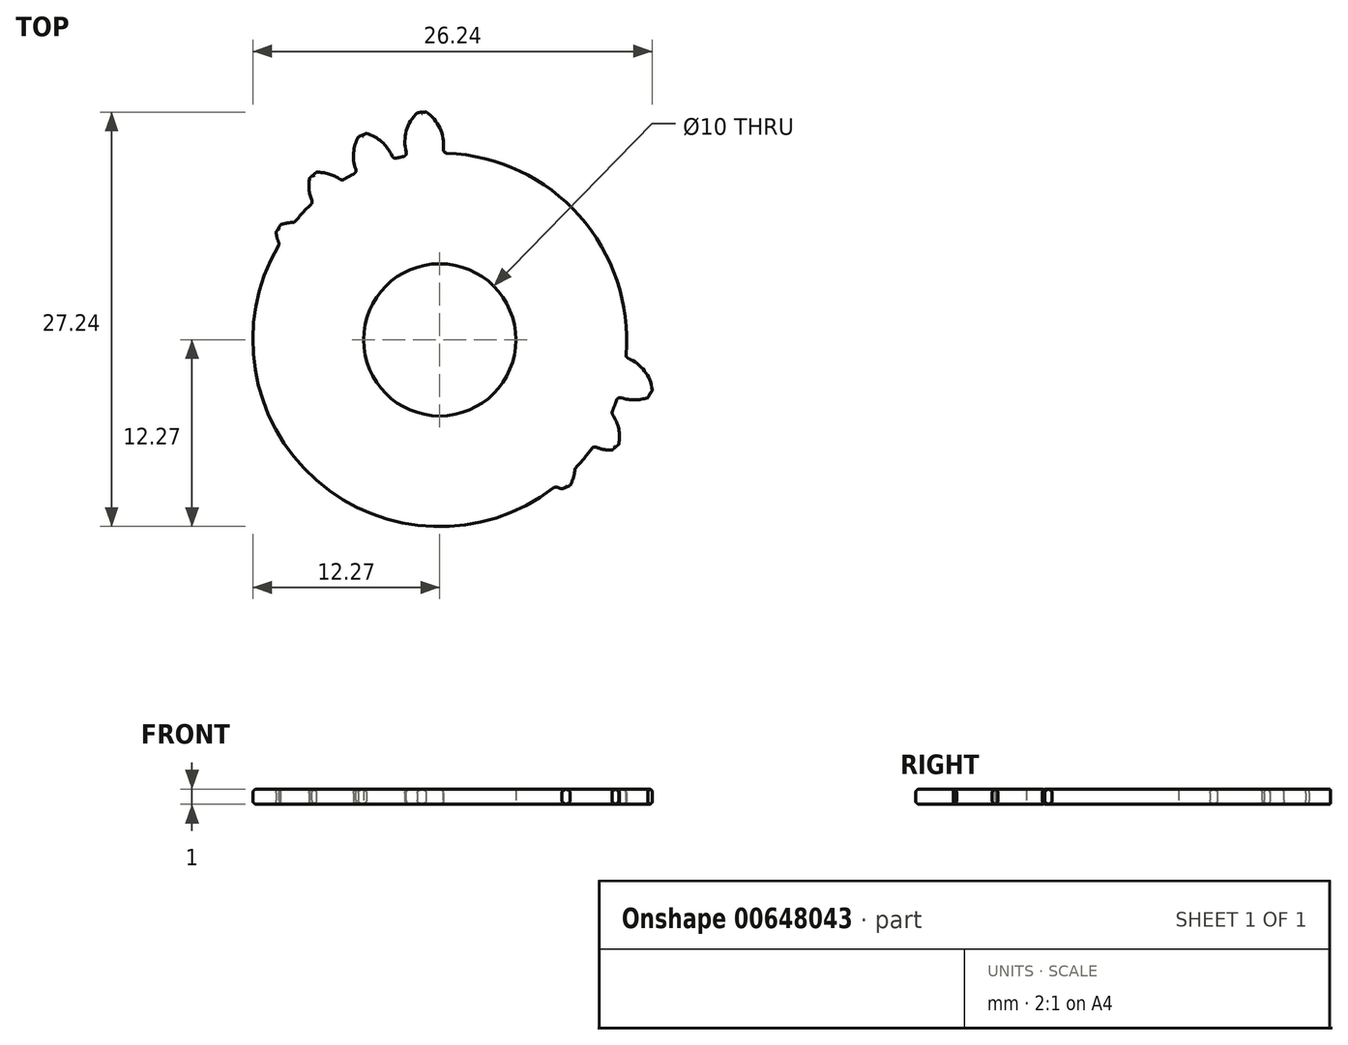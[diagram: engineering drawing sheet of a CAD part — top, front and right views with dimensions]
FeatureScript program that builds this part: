
annotation { "Feature Type Name" : "Feature", "Feature Type Description" : "" }
export const myFeature = defineFeature(function(context is Context, id is Id, definition is map)
    precondition{}
    {
        {
            assignVariable(context, id + "F0", {"name" : "GearDepth", "anyValue" : 1});
        }
        {
            assignVariable(context, id + "F1", {"name" : "TeethFillet", "anyValue" : getVariable(context, 'GearDepth') * .25});
        }
        {
            var Q0;
            Q0=qCreatedBy(makeId("Top.planeOp"),FACE);
            var sketch = newSketch(context, id + "F2", { "sketchPlane" : qUnion([Q0])});
            skCircle(sketch, "E0", {"center": v(0, 0) * mm, "radius": 12.27 * mm});
            skCircle(sketch, "E1", {"center": v(0, 0) * mm, "radius": 13.64 * mm, "construction": true});
            skCircle(sketch, "E2", {"center": v(0, 0) * mm, "radius": 15 * mm, "construction": true});
            skLineSegment(sketch, "E3", {"start": v(0, 0) * mm, "end": v(0, 17.6) * mm, "construction": true});
            skLineSegment(sketch, "E4", {"start": v(0, 0) * mm, "end": v(-1.42, 18) * mm, "construction": true});
            skLineSegment(sketch, "E5", {"start": v(0, 13.64) * mm, "end": v(-10.54, 13.64) * mm, "construction": true});
            skLineSegment(sketch, "E6", {"start": v(0, 13.64) * mm, "end": v(-10.3, 9.9) * mm, "construction": true});
            skCircle(sketch, "E7", {"center": v(0, 13.64) * mm, "radius": 3.4 * mm, "construction": true});
            skCircle(sketch, "E8", {"center": v(-3.2, 12.47) * mm, "radius": 3.4 * mm, "construction": true});
            skArc(sketch, "E9", {"start": v(-6.4, 13.64) * mm, "mid": v(-6.42, 13.6) * mm, "end": v(-6.44, 13.55) * mm});
            skArc(sketch, "E10.trimOffspring", {"start": v(0.2, 12.27) * mm, "mid": v(0.07, 13.79) * mm, "end": v(-0.89, 14.97) * mm});
            skArc(sketch, "E11.MirrorCS", {"start": v(-2.12, 12.09) * mm, "mid": v(-2.22, 13.6) * mm, "end": v(-1.46, 14.93) * mm});
            skLineSegment(sketch, "E12", {"start": v(-1.46, 14.93) * mm, "end": v(-0.89, 14.97) * mm});
            skArc(sketch, "E13.1.0", {"start": v(-2.94, 11.33) * mm, "mid": v(-3.54, 12.73) * mm, "end": v(-4.81, 13.56) * mm});
            skLineSegment(sketch, "E13.1.1", {"start": v(-5.35, 13.34) * mm, "end": v(-4.81, 13.56) * mm});
            skArc(sketch, "E13.1.2", {"start": v(-5.09, 10.44) * mm, "mid": v(-5.66, 11.85) * mm, "end": v(-5.35, 13.34) * mm});
            skArc(sketch, "E13.2.0", {"start": v(-5.64, 9.46) * mm, "mid": v(-6.64, 10.6) * mm, "end": v(-8.1, 11) * mm});
            skLineSegment(sketch, "E13.2.1", {"start": v(-8.55, 10.63) * mm, "end": v(-8.1, 11) * mm});
            skArc(sketch, "E13.2.2", {"start": v(-7.4, 7.95) * mm, "mid": v(-8.38, 9.12) * mm, "end": v(-8.55, 10.63) * mm});
            skArc(sketch, "E13.3.0", {"start": v(-7.63, 6.85) * mm, "mid": v(-8.93, 7.63) * mm, "end": v(-10.45, 7.56) * mm});
            skLineSegment(sketch, "E13.3.1", {"start": v(-10.75, 7.07) * mm, "end": v(-10.45, 7.56) * mm});
            skArc(sketch, "E13.3.2", {"start": v(-8.84, 4.87) * mm, "mid": v(-10.13, 5.68) * mm, "end": v(-10.75, 7.07) * mm});
            skArc(sketch, "E13.4.0", {"start": v(-8.7, 3.75) * mm, "mid": v(-10.2, 4.1) * mm, "end": v(-11.62, 3.55) * mm});
            skLineSegment(sketch, "E13.4.1", {"start": v(-11.75, 3) * mm, "end": v(-11.62, 3.55) * mm});
            skArc(sketch, "E13.4.2", {"start": v(-9.25, 1.5) * mm, "mid": v(-10.73, 1.86) * mm, "end": v(-11.75, 3) * mm});
            skArc(sketch, "E13.5.0", {"start": v(-8.78, 0.47) * mm, "mid": v(-10.3, 0.34) * mm, "end": v(-11.49, -0.61) * mm});
            skLineSegment(sketch, "E13.5.1", {"start": v(-11.44, -1.19) * mm, "end": v(-11.49, -0.61) * mm});
            skArc(sketch, "E13.5.2", {"start": v(-8.6, -1.84) * mm, "mid": v(-10.12, -1.95) * mm, "end": v(-11.44, -1.19) * mm});
            skArc(sketch, "E13.6.0", {"start": v(-7.84, -2.67) * mm, "mid": v(-9.24, -3.26) * mm, "end": v(-10.07, -4.54) * mm});
            skLineSegment(sketch, "E13.6.1", {"start": v(-9.85, -5.07) * mm, "end": v(-10.07, -4.54) * mm});
            skArc(sketch, "E13.6.2", {"start": v(-6.95, -4.81) * mm, "mid": v(-8.36, -5.38) * mm, "end": v(-9.85, -5.07) * mm});
            skArc(sketch, "E13.7.0", {"start": v(-5.97, -5.36) * mm, "mid": v(-7.12, -6.36) * mm, "end": v(-7.52, -7.83) * mm});
            skLineSegment(sketch, "E13.7.1", {"start": v(-7.14, -8.27) * mm, "end": v(-7.52, -7.83) * mm});
            skArc(sketch, "E13.7.2", {"start": v(-4.46, -7.13) * mm, "mid": v(-5.63, -8.1) * mm, "end": v(-7.14, -8.27) * mm});
            skArc(sketch, "E13.8.0", {"start": v(-3.36, -7.35) * mm, "mid": v(-4.15, -8.66) * mm, "end": v(-4.07, -10.18) * mm});
            skLineSegment(sketch, "E13.8.1", {"start": v(-3.58, -10.48) * mm, "end": v(-4.07, -10.18) * mm});
            skArc(sketch, "E13.8.2", {"start": v(-1.38, -8.57) * mm, "mid": v(-2.19, -9.86) * mm, "end": v(-3.58, -10.48) * mm});
            skArc(sketch, "E13.9.0", {"start": v(-0.27, -8.43) * mm, "mid": v(-0.6, -9.92) * mm, "end": v(-0.06, -11.34) * mm});
            skLineSegment(sketch, "E13.9.1", {"start": v(0.5, -11.48) * mm, "end": v(-0.06, -11.34) * mm});
            skArc(sketch, "E13.9.2", {"start": v(2, -8.98) * mm, "mid": v(1.63, -10.45) * mm, "end": v(0.5, -11.48) * mm});
            skArc(sketch, "E13.10.0", {"start": v(3.01, -8.5) * mm, "mid": v(3.15, -10.03) * mm, "end": v(4.1, -11.21) * mm});
            skLineSegment(sketch, "E13.10.1", {"start": v(4.68, -11.17) * mm, "end": v(4.1, -11.21) * mm});
            skArc(sketch, "E13.10.2", {"start": v(5.33, -8.33) * mm, "mid": v(5.44, -9.84) * mm, "end": v(4.68, -11.17) * mm});
            skArc(sketch, "E13.11.0", {"start": v(6.16, -7.56) * mm, "mid": v(6.75, -8.97) * mm, "end": v(8.03, -9.8) * mm});
            skLineSegment(sketch, "E13.11.1", {"start": v(8.56, -9.58) * mm, "end": v(8.03, -9.8) * mm});
            skArc(sketch, "E13.11.2", {"start": v(8.3, -6.68) * mm, "mid": v(8.87, -8.09) * mm, "end": v(8.56, -9.58) * mm});
            skArc(sketch, "E13.12.0", {"start": v(8.85, -5.7) * mm, "mid": v(9.85, -6.85) * mm, "end": v(11.32, -7.24) * mm});
            skLineSegment(sketch, "E13.12.1", {"start": v(11.76, -6.87) * mm, "end": v(11.32, -7.24) * mm});
            skArc(sketch, "E13.12.2", {"start": v(10.62, -4.19) * mm, "mid": v(11.6, -5.35) * mm, "end": v(11.76, -6.87) * mm});
            skArc(sketch, "E13.13.0", {"start": v(10.84, -3.09) * mm, "mid": v(12.14, -3.87) * mm, "end": v(13.67, -3.8) * mm});
            skLineSegment(sketch, "E13.13.1", {"start": v(13.97, -3.3) * mm, "end": v(13.67, -3.8) * mm});
            skArc(sketch, "E13.13.2", {"start": v(12.05, -1.1) * mm, "mid": v(13.35, -1.91) * mm, "end": v(13.97, -3.3) * mm});
            skArc(sketch, "E13.14.0", {"start": v(11.92, 0) * mm, "mid": v(13.4, -0.33) * mm, "end": v(14.83, 0.2) * mm});
            skLineSegment(sketch, "E13.14.1", {"start": v(14.96, 0.77) * mm, "end": v(14.83, 0.2) * mm});
            skArc(sketch, "E13.14.2", {"start": v(12.47, 2.27) * mm, "mid": v(13.94, 1.9) * mm, "end": v(14.96, 0.77) * mm});
            skArc(sketch, "E13.15.0", {"start": v(12, 3.29) * mm, "mid": v(13.51, 3.42) * mm, "end": v(14.7, 4.38) * mm});
            skLineSegment(sketch, "E13.15.1", {"start": v(14.65, 4.95) * mm, "end": v(14.7, 4.38) * mm});
            skArc(sketch, "E13.15.2", {"start": v(11.81, 5.6) * mm, "mid": v(13.33, 5.71) * mm, "end": v(14.65, 4.95) * mm});
            skArc(sketch, "E13.16.0", {"start": v(11.05, 6.43) * mm, "mid": v(12.45, 7.03) * mm, "end": v(13.29, 8.3) * mm});
            skLineSegment(sketch, "E13.16.1", {"start": v(13.07, 8.83) * mm, "end": v(13.29, 8.3) * mm});
            skArc(sketch, "E13.16.2", {"start": v(10.16, 8.58) * mm, "mid": v(11.58, 9.15) * mm, "end": v(13.07, 8.83) * mm});
            skArc(sketch, "E13.17.0", {"start": v(9.19, 9.13) * mm, "mid": v(10.33, 10.13) * mm, "end": v(10.73, 11.6) * mm});
            skLineSegment(sketch, "E13.17.1", {"start": v(10.36, 12.03) * mm, "end": v(10.73, 11.6) * mm});
            skArc(sketch, "E13.17.2", {"start": v(7.68, 10.9) * mm, "mid": v(8.84, 11.87) * mm, "end": v(10.36, 12.03) * mm});
            skArc(sketch, "E13.18.0", {"start": v(6.58, 11.11) * mm, "mid": v(7.36, 12.42) * mm, "end": v(7.28, 13.94) * mm});
            skLineSegment(sketch, "E13.18.1", {"start": v(6.8, 14.24) * mm, "end": v(7.28, 13.94) * mm});
            skArc(sketch, "E13.18.2", {"start": v(4.6, 12.33) * mm, "mid": v(5.4, 13.62) * mm, "end": v(6.8, 14.24) * mm});
            skArc(sketch, "E13.19.0", {"start": v(3.48, 12.2) * mm, "mid": v(3.82, 13.68) * mm, "end": v(3.28, 15.1) * mm});
            skLineSegment(sketch, "E13.19.1", {"start": v(2.72, 15.24) * mm, "end": v(3.28, 15.1) * mm});
            skArc(sketch, "E13.19.2", {"start": v(1.22, 12.74) * mm, "mid": v(1.59, 14.22) * mm, "end": v(2.72, 15.24) * mm});
            skPoint(sketch, "E13.center", {"position": v(1.6, 1.88) * mm});
            skCircle(sketch, "E14", {"center": v(0, 0) * mm, "radius": 5 * mm});
            skSolve(sketch);
        }
        {
            var Q0;
            {var subQ0=sQuery(id+"F2.wireOp",EDGE,"E10.trimOffspring");Q0=makeQuery(id+"F2.imprint","IMPRINT",FACE,{"disambiguationData":[TD([[makeQuery(id+"F2.imprint","IMPRINT",EDGE,{"derivedFrom":subQ0}),1.0]])]});}
            var Q1;
            {var subQ0=sQuery(id+"F2.wireOp",EDGE,"E0");var subQ1=makeQuery(id+"F2.imprint","INTERSECT",VERTEX,{"derivedFrom":[subQ0,sQuery(id+"F2.wireOp",EDGE,"E10.trimOffspring")]});Q1=makeQuery(id+"F2.imprint","IMPRINT",FACE,{"disambiguationData":[TD([[makeQuery(id+"F2.imprint","IMPRINT",EDGE,{"disambiguationData":[TD([[subQ1,-1.0]])],"derivedFrom":subQ0}),1.0]])]});}
            var Q2;
            {var subQ0=sQuery(id+"F2.wireOp",EDGE,"E13.1.0");Q2=makeQuery(id+"F2.imprint","IMPRINT",FACE,{"disambiguationData":[TD([[makeQuery(id+"F2.imprint","IMPRINT",EDGE,{"derivedFrom":subQ0}),1.0]])]});}
            var Q3;
            {var subQ0=sQuery(id+"F2.wireOp",EDGE,"E13.2.0");Q3=makeQuery(id+"F2.imprint","IMPRINT",FACE,{"disambiguationData":[TD([[makeQuery(id+"F2.imprint","IMPRINT",EDGE,{"derivedFrom":subQ0}),1.0]])]});}
            var Q4;
            {var subQ0=sQuery(id+"F2.wireOp",EDGE,"E13.3.0");Q4=makeQuery(id+"F2.imprint","IMPRINT",FACE,{"disambiguationData":[TD([[makeQuery(id+"F2.imprint","IMPRINT",EDGE,{"derivedFrom":subQ0}),1.0]])]});}
            var Q5;
            {var subQ0=sQuery(id+"F2.wireOp",EDGE,"E13.4.0");Q5=makeQuery(id+"F2.imprint","IMPRINT",FACE,{"disambiguationData":[TD([[makeQuery(id+"F2.imprint","IMPRINT",EDGE,{"derivedFrom":subQ0}),1.0]])]});}
            var Q6;
            {var subQ0=sQuery(id+"F2.wireOp",EDGE,"E13.5.0");Q6=makeQuery(id+"F2.imprint","IMPRINT",FACE,{"disambiguationData":[TD([[makeQuery(id+"F2.imprint","IMPRINT",EDGE,{"derivedFrom":subQ0}),1.0]])]});}
            var Q7;
            {var subQ0=sQuery(id+"F2.wireOp",EDGE,"E13.6.0");Q7=makeQuery(id+"F2.imprint","IMPRINT",FACE,{"disambiguationData":[TD([[makeQuery(id+"F2.imprint","IMPRINT",EDGE,{"derivedFrom":subQ0}),1.0]])]});}
            var Q8;
            {var subQ0=sQuery(id+"F2.wireOp",EDGE,"E13.7.0");Q8=makeQuery(id+"F2.imprint","IMPRINT",FACE,{"disambiguationData":[TD([[makeQuery(id+"F2.imprint","IMPRINT",EDGE,{"derivedFrom":subQ0}),1.0]])]});}
            var Q9;
            {var subQ0=sQuery(id+"F2.wireOp",EDGE,"E13.8.0");Q9=makeQuery(id+"F2.imprint","IMPRINT",FACE,{"disambiguationData":[TD([[makeQuery(id+"F2.imprint","IMPRINT",EDGE,{"derivedFrom":subQ0}),1.0]])]});}
            var Q10;
            {var subQ0=sQuery(id+"F2.wireOp",EDGE,"E13.9.0");Q10=makeQuery(id+"F2.imprint","IMPRINT",FACE,{"disambiguationData":[TD([[makeQuery(id+"F2.imprint","IMPRINT",EDGE,{"derivedFrom":subQ0}),1.0]])]});}
            var Q11;
            {var subQ0=sQuery(id+"F2.wireOp",EDGE,"E13.10.0");Q11=makeQuery(id+"F2.imprint","IMPRINT",FACE,{"disambiguationData":[TD([[makeQuery(id+"F2.imprint","IMPRINT",EDGE,{"derivedFrom":subQ0}),1.0]])]});}
            var Q12;
            {var subQ0=sQuery(id+"F2.wireOp",EDGE,"E13.11.0");Q12=makeQuery(id+"F2.imprint","IMPRINT",FACE,{"disambiguationData":[TD([[makeQuery(id+"F2.imprint","IMPRINT",EDGE,{"derivedFrom":subQ0}),1.0]])]});}
            var Q13;
            {var subQ0=sQuery(id+"F2.wireOp",EDGE,"E13.12.0");Q13=makeQuery(id+"F2.imprint","IMPRINT",FACE,{"disambiguationData":[TD([[makeQuery(id+"F2.imprint","IMPRINT",EDGE,{"derivedFrom":subQ0}),1.0]])]});}
            var Q14;
            {var subQ0=sQuery(id+"F2.wireOp",EDGE,"E13.13.0");Q14=makeQuery(id+"F2.imprint","IMPRINT",FACE,{"disambiguationData":[TD([[makeQuery(id+"F2.imprint","IMPRINT",EDGE,{"derivedFrom":subQ0}),1.0]])]});}
            var Q15;
            {var subQ0=sQuery(id+"F2.wireOp",EDGE,"E13.14.0");Q15=makeQuery(id+"F2.imprint","IMPRINT",FACE,{"disambiguationData":[TD([[makeQuery(id+"F2.imprint","IMPRINT",EDGE,{"derivedFrom":subQ0}),1.0]])]});}
            var Q16;
            {var subQ0=sQuery(id+"F2.wireOp",EDGE,"E13.15.0");Q16=makeQuery(id+"F2.imprint","IMPRINT",FACE,{"disambiguationData":[TD([[makeQuery(id+"F2.imprint","IMPRINT",EDGE,{"derivedFrom":subQ0}),1.0]])]});}
            var Q17;
            {var subQ0=sQuery(id+"F2.wireOp",EDGE,"E13.16.0");Q17=makeQuery(id+"F2.imprint","IMPRINT",FACE,{"disambiguationData":[TD([[makeQuery(id+"F2.imprint","IMPRINT",EDGE,{"derivedFrom":subQ0}),1.0]])]});}
            var Q18;
            {var subQ0=sQuery(id+"F2.wireOp",EDGE,"E13.17.0");Q18=makeQuery(id+"F2.imprint","IMPRINT",FACE,{"disambiguationData":[TD([[makeQuery(id+"F2.imprint","IMPRINT",EDGE,{"derivedFrom":subQ0}),1.0]])]});}
            var Q19;
            {var subQ0=sQuery(id+"F2.wireOp",EDGE,"E13.18.0");Q19=makeQuery(id+"F2.imprint","IMPRINT",FACE,{"disambiguationData":[TD([[makeQuery(id+"F2.imprint","IMPRINT",EDGE,{"derivedFrom":subQ0}),1.0]])]});}
            var Q20;
            {var subQ0=sQuery(id+"F2.wireOp",EDGE,"E13.19.0");Q20=makeQuery(id+"F2.imprint","IMPRINT",FACE,{"disambiguationData":[TD([[makeQuery(id+"F2.imprint","IMPRINT",EDGE,{"derivedFrom":subQ0}),1.0]])]});}
            var Q21;
            Q21=sQuery(id+"F2.wireOp",EDGE,"E0");
            var Q22;
            Q22=sQuery(id+"F2.wireOp",EDGE,"E10.trimOffspring");
            var Q23;
            Q23=sQuery(id+"F2.wireOp",EDGE,"E12");
            var Q24;
            Q24=sQuery(id+"F2.wireOp",EDGE,"E11.MirrorCS");
            extrude(context, id + "F3", {"entities" : qUnion([Q0, Q1, Q2, Q3, Q4, Q5, Q6, Q7, Q8, Q9, Q10, Q11, Q12, Q13, Q14, Q15, Q16, Q17, Q18, Q19, Q20]), "surfaceEntities" : qUnion([Q21, Q22, Q23, Q24]), "depth" : (getVariable(context, 'GearDepth')) * mm, "offsetDistance" : 25 * mm});
        }
        {
            var Q0;
            Q0=makeQuery(id+"F3.opExtrude","CAP_EDGE",EDGE,{"disambiguationData":[OSD([sQuery(id+"F2.wireOp",EDGE,"E13.5.2")])],"isStart":false});
            var Q1;
            Q1=makeQuery(id+"F3.opExtrude","CAP_EDGE",EDGE,{"disambiguationData":[OSD([sQuery(id+"F2.wireOp",EDGE,"E13.5.1")])],"isStart":false});
            var Q2;
            {var subQ0=sQuery(id+"F2.wireOp",EDGE,"E0");Q2=makeQuery(id+"F3.opExtrude","CAP_EDGE",EDGE,{"disambiguationData":[OSD([subQ0]),TDD([makeQuery(id+"F2.imprint","IMPRINT",EDGE,{"disambiguationData":[TD([[makeQuery(id+"F2.imprint","INTERSECT",VERTEX,{"derivedFrom":[subQ0,sQuery(id+"F2.wireOp",EDGE,"E13.5.2")]}),-1.0]])],"derivedFrom":subQ0})])],"isStart":false});}
            var Q3;
            Q3=makeQuery(id+"F3.opExtrude","CAP_EDGE",EDGE,{"disambiguationData":[OSD([sQuery(id+"F2.wireOp",EDGE,"E13.6.0")])],"isStart":false});
            var Q4;
            Q4=makeQuery(id+"F3.opExtrude","CAP_EDGE",EDGE,{"disambiguationData":[OSD([sQuery(id+"F2.wireOp",EDGE,"E13.6.1")])],"isStart":false});
            var Q5;
            Q5=makeQuery(id+"F3.opExtrude","CAP_EDGE",EDGE,{"disambiguationData":[OSD([sQuery(id+"F2.wireOp",EDGE,"E13.6.2")])],"isStart":false});
            var Q6;
            {var subQ0=sQuery(id+"F2.wireOp",EDGE,"E0");Q6=makeQuery(id+"F3.opExtrude","SWEPT_FACE",FACE,{"disambiguationData":[OSD([subQ0]),TDD([makeQuery(id+"F2.imprint","IMPRINT",EDGE,{"disambiguationData":[TD([[makeQuery(id+"F2.imprint","INTERSECT",VERTEX,{"derivedFrom":[subQ0,sQuery(id+"F2.wireOp",EDGE,"E13.6.2")]}),-1.0]])],"derivedFrom":subQ0})])]});}
            var Q7;
            {var subQ0=sQuery(id+"F2.wireOp",EDGE,"E0");Q7=makeQuery(id+"F3.opExtrude","CAP_EDGE",EDGE,{"disambiguationData":[OSD([subQ0]),TDD([makeQuery(id+"F2.imprint","IMPRINT",EDGE,{"disambiguationData":[TD([[makeQuery(id+"F2.imprint","INTERSECT",VERTEX,{"derivedFrom":[subQ0,sQuery(id+"F2.wireOp",EDGE,"E13.6.2")]}),-1.0]])],"derivedFrom":subQ0})])],"isStart":false});}
            var Q8;
            Q8=makeQuery(id+"F3.opExtrude","CAP_EDGE",EDGE,{"disambiguationData":[OSD([sQuery(id+"F2.wireOp",EDGE,"E13.7.2")])],"isStart":true});
            var Q9;
            {var subQ0=sQuery(id+"F2.wireOp",EDGE,"E0");Q9=makeQuery(id+"F3.opExtrude","CAP_EDGE",EDGE,{"disambiguationData":[OSD([subQ0]),TDD([makeQuery(id+"F2.imprint","IMPRINT",EDGE,{"disambiguationData":[TD([[makeQuery(id+"F2.imprint","INTERSECT",VERTEX,{"derivedFrom":[subQ0,sQuery(id+"F2.wireOp",EDGE,"E13.7.2")]}),-1.0]])],"derivedFrom":subQ0})])],"isStart":true});}
            var Q10;
            Q10=makeQuery(id+"F3.opExtrude","CAP_EDGE",EDGE,{"disambiguationData":[OSD([sQuery(id+"F2.wireOp",EDGE,"E13.7.2")])],"isStart":false});
            var Q11;
            {var subQ0=sQuery(id+"F2.wireOp",EDGE,"E0");Q11=makeQuery(id+"F3.opExtrude","CAP_EDGE",EDGE,{"disambiguationData":[OSD([subQ0]),TDD([makeQuery(id+"F2.imprint","IMPRINT",EDGE,{"disambiguationData":[TD([[makeQuery(id+"F2.imprint","INTERSECT",VERTEX,{"derivedFrom":[subQ0,sQuery(id+"F2.wireOp",EDGE,"E13.7.2")]}),-1.0]])],"derivedFrom":subQ0})])],"isStart":false});}
            var Q12;
            Q12=makeQuery(id+"F3.opExtrude","CAP_EDGE",EDGE,{"disambiguationData":[OSD([sQuery(id+"F2.wireOp",EDGE,"E13.8.0")])],"isStart":false});
            var Q13;
            {var subQ0=sQuery(id+"F2.wireOp",EDGE,"E0");Q13=makeQuery(id+"F3.opExtrude","SWEPT_FACE",FACE,{"disambiguationData":[OSD([subQ0]),TDD([makeQuery(id+"F2.imprint","IMPRINT",EDGE,{"disambiguationData":[TD([[makeQuery(id+"F2.imprint","INTERSECT",VERTEX,{"derivedFrom":[subQ0,sQuery(id+"F2.wireOp",EDGE,"E13.7.2")]}),-1.0]])],"derivedFrom":subQ0})])]});}
            var Q14;
            Q14=makeQuery(id+"F3.opExtrude","CAP_EDGE",EDGE,{"disambiguationData":[OSD([sQuery(id+"F2.wireOp",EDGE,"E13.6.0")])],"isStart":true});
            var Q15;
            Q15=makeQuery(id+"F3.opExtrude","CAP_EDGE",EDGE,{"disambiguationData":[OSD([sQuery(id+"F2.wireOp",EDGE,"E13.8.2")])],"isStart":false});
            var Q16;
            {var subQ0=sQuery(id+"F2.wireOp",EDGE,"E0");Q16=makeQuery(id+"F3.opExtrude","CAP_EDGE",EDGE,{"disambiguationData":[OSD([subQ0]),TDD([makeQuery(id+"F2.imprint","IMPRINT",EDGE,{"disambiguationData":[TD([[makeQuery(id+"F2.imprint","INTERSECT",VERTEX,{"derivedFrom":[subQ0,sQuery(id+"F2.wireOp",EDGE,"E13.8.2")]}),-1.0]])],"derivedFrom":subQ0})])],"isStart":false});}
            var Q17;
            Q17=makeQuery(id+"F3.opExtrude","CAP_EDGE",EDGE,{"disambiguationData":[OSD([sQuery(id+"F2.wireOp",EDGE,"E13.9.0")])],"isStart":false});
            var Q18;
            Q18=makeQuery(id+"F3.opExtrude","CAP_EDGE",EDGE,{"disambiguationData":[OSD([sQuery(id+"F2.wireOp",EDGE,"E13.9.2")])],"isStart":false});
            var Q19;
            {var subQ0=sQuery(id+"F2.wireOp",EDGE,"E0");Q19=makeQuery(id+"F3.opExtrude","CAP_EDGE",EDGE,{"disambiguationData":[OSD([subQ0]),TDD([makeQuery(id+"F2.imprint","IMPRINT",EDGE,{"disambiguationData":[TD([[makeQuery(id+"F2.imprint","INTERSECT",VERTEX,{"derivedFrom":[subQ0,sQuery(id+"F2.wireOp",EDGE,"E13.9.2")]}),-1.0]])],"derivedFrom":subQ0})])],"isStart":false});}
            var Q20;
            Q20=makeQuery(id+"F3.opExtrude","CAP_EDGE",EDGE,{"disambiguationData":[OSD([sQuery(id+"F2.wireOp",EDGE,"E13.10.0")])],"isStart":false});
            var Q21;
            Q21=makeQuery(id+"F3.opExtrude","CAP_EDGE",EDGE,{"disambiguationData":[OSD([sQuery(id+"F2.wireOp",EDGE,"E13.10.2")])],"isStart":false});
            var Q22;
            {var subQ0=sQuery(id+"F2.wireOp",EDGE,"E0");Q22=makeQuery(id+"F3.opExtrude","CAP_EDGE",EDGE,{"disambiguationData":[OSD([subQ0]),TDD([makeQuery(id+"F2.imprint","IMPRINT",EDGE,{"disambiguationData":[TD([[makeQuery(id+"F2.imprint","INTERSECT",VERTEX,{"derivedFrom":[subQ0,sQuery(id+"F2.wireOp",EDGE,"E13.10.2")]}),-1.0]])],"derivedFrom":subQ0})])],"isStart":false});}
            var Q23;
            Q23=makeQuery(id+"F3.opExtrude","CAP_EDGE",EDGE,{"disambiguationData":[OSD([sQuery(id+"F2.wireOp",EDGE,"E13.11.0")])],"isStart":false});
            var Q24;
            Q24=makeQuery(id+"F3.opExtrude","CAP_EDGE",EDGE,{"disambiguationData":[OSD([sQuery(id+"F2.wireOp",EDGE,"E13.11.2")])],"isStart":false});
            var Q25;
            {var subQ0=sQuery(id+"F2.wireOp",EDGE,"E0");Q25=makeQuery(id+"F3.opExtrude","CAP_EDGE",EDGE,{"disambiguationData":[OSD([subQ0]),TDD([makeQuery(id+"F2.imprint","IMPRINT",EDGE,{"disambiguationData":[TD([[makeQuery(id+"F2.imprint","INTERSECT",VERTEX,{"derivedFrom":[subQ0,sQuery(id+"F2.wireOp",EDGE,"E13.11.2")]}),-1.0]])],"derivedFrom":subQ0})])],"isStart":false});}
            var Q26;
            Q26=makeQuery(id+"F3.opExtrude","CAP_EDGE",EDGE,{"disambiguationData":[OSD([sQuery(id+"F2.wireOp",EDGE,"E13.12.0")])],"isStart":false});
            var Q27;
            Q27=makeQuery(id+"F3.opExtrude","CAP_EDGE",EDGE,{"disambiguationData":[OSD([sQuery(id+"F2.wireOp",EDGE,"E13.12.2")])],"isStart":false});
            var Q28;
            {var subQ0=sQuery(id+"F2.wireOp",EDGE,"E0");Q28=makeQuery(id+"F3.opExtrude","CAP_EDGE",EDGE,{"disambiguationData":[OSD([subQ0]),TDD([makeQuery(id+"F2.imprint","IMPRINT",EDGE,{"disambiguationData":[TD([[makeQuery(id+"F2.imprint","INTERSECT",VERTEX,{"derivedFrom":[subQ0,sQuery(id+"F2.wireOp",EDGE,"E13.12.2")]}),-1.0]])],"derivedFrom":subQ0})])],"isStart":false});}
            var Q29;
            Q29=makeQuery(id+"F3.opExtrude","CAP_EDGE",EDGE,{"disambiguationData":[OSD([sQuery(id+"F2.wireOp",EDGE,"E13.13.0")])],"isStart":false});
            var Q30;
            Q30=makeQuery(id+"F3.opExtrude","CAP_EDGE",EDGE,{"disambiguationData":[OSD([sQuery(id+"F2.wireOp",EDGE,"E13.13.2")])],"isStart":false});
            var Q31;
            {var subQ0=sQuery(id+"F2.wireOp",EDGE,"E0");Q31=makeQuery(id+"F3.opExtrude","CAP_EDGE",EDGE,{"disambiguationData":[OSD([subQ0]),TDD([makeQuery(id+"F2.imprint","IMPRINT",EDGE,{"disambiguationData":[TD([[makeQuery(id+"F2.imprint","INTERSECT",VERTEX,{"derivedFrom":[subQ0,sQuery(id+"F2.wireOp",EDGE,"E13.13.2")]}),-1.0]])],"derivedFrom":subQ0})])],"isStart":false});}
            var Q32;
            Q32=makeQuery(id+"F3.opExtrude","CAP_EDGE",EDGE,{"disambiguationData":[OSD([sQuery(id+"F2.wireOp",EDGE,"E13.14.0")])],"isStart":false});
            var Q33;
            Q33=makeQuery(id+"F3.opExtrude","CAP_EDGE",EDGE,{"disambiguationData":[OSD([sQuery(id+"F2.wireOp",EDGE,"E13.14.2")])],"isStart":false});
            var Q34;
            {var subQ0=sQuery(id+"F2.wireOp",EDGE,"E0");Q34=makeQuery(id+"F3.opExtrude","CAP_EDGE",EDGE,{"disambiguationData":[OSD([subQ0]),TDD([makeQuery(id+"F2.imprint","IMPRINT",EDGE,{"disambiguationData":[TD([[makeQuery(id+"F2.imprint","INTERSECT",VERTEX,{"derivedFrom":[subQ0,sQuery(id+"F2.wireOp",EDGE,"E13.14.2")]}),-1.0]])],"derivedFrom":subQ0})])],"isStart":false});}
            var Q35;
            Q35=makeQuery(id+"F3.opExtrude","CAP_EDGE",EDGE,{"disambiguationData":[OSD([sQuery(id+"F2.wireOp",EDGE,"E13.15.0")])],"isStart":false});
            var Q36;
            {var subQ0=sQuery(id+"F2.wireOp",EDGE,"E0");Q36=makeQuery(id+"F3.opExtrude","CAP_EDGE",EDGE,{"disambiguationData":[OSD([subQ0]),TDD([makeQuery(id+"F2.imprint","IMPRINT",EDGE,{"disambiguationData":[TD([[makeQuery(id+"F2.imprint","INTERSECT",VERTEX,{"derivedFrom":[subQ0,sQuery(id+"F2.wireOp",EDGE,"E13.14.2")]}),-1.0]])],"derivedFrom":subQ0})])],"isStart":false});}
            var Q37;
            Q37=makeQuery(id+"F3.opExtrude","CAP_EDGE",EDGE,{"disambiguationData":[OSD([sQuery(id+"F2.wireOp",EDGE,"E13.15.2")])],"isStart":false});
            var Q38;
            {var subQ0=sQuery(id+"F2.wireOp",EDGE,"E0");Q38=makeQuery(id+"F3.opExtrude","CAP_EDGE",EDGE,{"disambiguationData":[OSD([subQ0]),TDD([makeQuery(id+"F2.imprint","IMPRINT",EDGE,{"disambiguationData":[TD([[makeQuery(id+"F2.imprint","INTERSECT",VERTEX,{"derivedFrom":[subQ0,sQuery(id+"F2.wireOp",EDGE,"E13.15.2")]}),-1.0]])],"derivedFrom":subQ0})])],"isStart":false});}
            var Q39;
            Q39=makeQuery(id+"F3.opExtrude","CAP_EDGE",EDGE,{"disambiguationData":[OSD([sQuery(id+"F2.wireOp",EDGE,"E13.16.0")])],"isStart":false});
            var Q40;
            Q40=makeQuery(id+"F3.opExtrude","CAP_EDGE",EDGE,{"disambiguationData":[OSD([sQuery(id+"F2.wireOp",EDGE,"E13.16.2")])],"isStart":false});
            var Q41;
            Q41=makeQuery(id+"F3.opExtrude","CAP_EDGE",EDGE,{"disambiguationData":[OSD([sQuery(id+"F2.wireOp",EDGE,"E13.17.0")])],"isStart":false});
            var Q42;
            {var subQ0=sQuery(id+"F2.wireOp",EDGE,"E0");Q42=makeQuery(id+"F3.opExtrude","CAP_EDGE",EDGE,{"disambiguationData":[OSD([subQ0]),TDD([makeQuery(id+"F2.imprint","IMPRINT",EDGE,{"disambiguationData":[TD([[makeQuery(id+"F2.imprint","INTERSECT",VERTEX,{"derivedFrom":[subQ0,sQuery(id+"F2.wireOp",EDGE,"E13.16.2")]}),-1.0]])],"derivedFrom":subQ0})])],"isStart":false});}
            var Q43;
            Q43=makeQuery(id+"F3.opExtrude","CAP_EDGE",EDGE,{"disambiguationData":[OSD([sQuery(id+"F2.wireOp",EDGE,"E13.17.2")])],"isStart":false});
            var Q44;
            {var subQ0=sQuery(id+"F2.wireOp",EDGE,"E0");Q44=makeQuery(id+"F3.opExtrude","CAP_EDGE",EDGE,{"disambiguationData":[OSD([subQ0]),TDD([makeQuery(id+"F2.imprint","IMPRINT",EDGE,{"disambiguationData":[TD([[makeQuery(id+"F2.imprint","INTERSECT",VERTEX,{"derivedFrom":[subQ0,sQuery(id+"F2.wireOp",EDGE,"E13.17.2")]}),-1.0]])],"derivedFrom":subQ0})])],"isStart":false});}
            var Q45;
            Q45=makeQuery(id+"F3.opExtrude","CAP_EDGE",EDGE,{"disambiguationData":[OSD([sQuery(id+"F2.wireOp",EDGE,"E13.18.0")])],"isStart":false});
            var Q46;
            Q46=makeQuery(id+"F3.opExtrude","CAP_EDGE",EDGE,{"disambiguationData":[OSD([sQuery(id+"F2.wireOp",EDGE,"E13.18.2")])],"isStart":false});
            var Q47;
            {var subQ0=sQuery(id+"F2.wireOp",EDGE,"E0");Q47=makeQuery(id+"F3.opExtrude","CAP_EDGE",EDGE,{"disambiguationData":[OSD([subQ0]),TDD([makeQuery(id+"F2.imprint","IMPRINT",EDGE,{"disambiguationData":[TD([[makeQuery(id+"F2.imprint","INTERSECT",VERTEX,{"derivedFrom":[subQ0,sQuery(id+"F2.wireOp",EDGE,"E13.18.2")]}),-1.0]])],"derivedFrom":subQ0})])],"isStart":false});}
            var Q48;
            Q48=makeQuery(id+"F3.opExtrude","CAP_EDGE",EDGE,{"disambiguationData":[OSD([sQuery(id+"F2.wireOp",EDGE,"E13.19.0")])],"isStart":false});
            var Q49;
            Q49=makeQuery(id+"F3.opExtrude","CAP_EDGE",EDGE,{"disambiguationData":[OSD([sQuery(id+"F2.wireOp",EDGE,"E13.19.2")])],"isStart":false});
            var Q50;
            Q50=makeQuery(id+"F3.opExtrude","CAP_EDGE",EDGE,{"disambiguationData":[OSD([sQuery(id+"F2.wireOp",EDGE,"E10.trimOffspring")])],"isStart":false});
            var Q51;
            Q51=makeQuery(id+"F3.opExtrude","CAP_EDGE",EDGE,{"disambiguationData":[OSD([sQuery(id+"F2.wireOp",EDGE,"E11.MirrorCS")])],"isStart":false});
            var Q52;
            {var subQ0=sQuery(id+"F2.wireOp",EDGE,"E0");Q52=makeQuery(id+"F3.opExtrude","CAP_EDGE",EDGE,{"disambiguationData":[OSD([subQ0]),TDD([makeQuery(id+"F2.imprint","IMPRINT",EDGE,{"disambiguationData":[TD([[makeQuery(id+"F2.imprint","INTERSECT",VERTEX,{"derivedFrom":[subQ0,sQuery(id+"F2.wireOp",EDGE,"E11.MirrorCS")]}),-1.0]])],"derivedFrom":subQ0})])],"isStart":false});}
            var Q53;
            Q53=makeQuery(id+"F3.opExtrude","CAP_EDGE",EDGE,{"disambiguationData":[OSD([sQuery(id+"F2.wireOp",EDGE,"E13.1.0")])],"isStart":false});
            var Q54;
            Q54=makeQuery(id+"F3.opExtrude","CAP_EDGE",EDGE,{"disambiguationData":[OSD([sQuery(id+"F2.wireOp",EDGE,"E13.1.2")])],"isStart":false});
            var Q55;
            {var subQ0=sQuery(id+"F2.wireOp",EDGE,"E0");Q55=makeQuery(id+"F3.opExtrude","CAP_EDGE",EDGE,{"disambiguationData":[OSD([subQ0]),TDD([makeQuery(id+"F2.imprint","IMPRINT",EDGE,{"disambiguationData":[TD([[makeQuery(id+"F2.imprint","INTERSECT",VERTEX,{"derivedFrom":[subQ0,sQuery(id+"F2.wireOp",EDGE,"E13.1.2")]}),-1.0]])],"derivedFrom":subQ0})])],"isStart":false});}
            var Q56;
            Q56=makeQuery(id+"F3.opExtrude","CAP_EDGE",EDGE,{"disambiguationData":[OSD([sQuery(id+"F2.wireOp",EDGE,"E13.2.0")])],"isStart":false});
            var Q57;
            Q57=makeQuery(id+"F3.opExtrude","CAP_EDGE",EDGE,{"disambiguationData":[OSD([sQuery(id+"F2.wireOp",EDGE,"E13.2.2")])],"isStart":false});
            var Q58;
            {var subQ0=sQuery(id+"F2.wireOp",EDGE,"E0");Q58=makeQuery(id+"F3.opExtrude","CAP_EDGE",EDGE,{"disambiguationData":[OSD([subQ0]),TDD([makeQuery(id+"F2.imprint","IMPRINT",EDGE,{"disambiguationData":[TD([[makeQuery(id+"F2.imprint","INTERSECT",VERTEX,{"derivedFrom":[subQ0,sQuery(id+"F2.wireOp",EDGE,"E13.2.2")]}),-1.0]])],"derivedFrom":subQ0})])],"isStart":false});}
            var Q59;
            Q59=makeQuery(id+"F3.opExtrude","CAP_EDGE",EDGE,{"disambiguationData":[OSD([sQuery(id+"F2.wireOp",EDGE,"E13.3.0")])],"isStart":false});
            var Q60;
            Q60=makeQuery(id+"F3.opExtrude","CAP_EDGE",EDGE,{"disambiguationData":[OSD([sQuery(id+"F2.wireOp",EDGE,"E13.3.2")])],"isStart":false});
            var Q61;
            {var subQ0=sQuery(id+"F2.wireOp",EDGE,"E0");Q61=makeQuery(id+"F3.opExtrude","CAP_EDGE",EDGE,{"disambiguationData":[OSD([subQ0]),TDD([makeQuery(id+"F2.imprint","IMPRINT",EDGE,{"disambiguationData":[TD([[makeQuery(id+"F2.imprint","INTERSECT",VERTEX,{"derivedFrom":[subQ0,sQuery(id+"F2.wireOp",EDGE,"E13.3.2")]}),-1.0]])],"derivedFrom":subQ0})])],"isStart":false});}
            var Q62;
            Q62=makeQuery(id+"F3.opExtrude","CAP_EDGE",EDGE,{"disambiguationData":[OSD([sQuery(id+"F2.wireOp",EDGE,"E13.4.0")])],"isStart":false});
            var Q63;
            Q63=makeQuery(id+"F3.opExtrude","CAP_EDGE",EDGE,{"disambiguationData":[OSD([sQuery(id+"F2.wireOp",EDGE,"E13.4.2")])],"isStart":false});
            var Q64;
            {var subQ0=sQuery(id+"F2.wireOp",EDGE,"E0");Q64=makeQuery(id+"F3.opExtrude","CAP_EDGE",EDGE,{"disambiguationData":[OSD([subQ0]),TDD([makeQuery(id+"F2.imprint","IMPRINT",EDGE,{"disambiguationData":[TD([[makeQuery(id+"F2.imprint","INTERSECT",VERTEX,{"derivedFrom":[subQ0,sQuery(id+"F2.wireOp",EDGE,"E13.4.2")]}),-1.0]])],"derivedFrom":subQ0})])],"isStart":false});}
            var Q65;
            {var subQ0=sQuery(id+"F2.wireOp",EDGE,"E0");Q65=makeQuery(id+"F3.opExtrude","CAP_EDGE",EDGE,{"disambiguationData":[OSD([subQ0]),TDD([makeQuery(id+"F2.imprint","IMPRINT",EDGE,{"disambiguationData":[TD([[makeQuery(id+"F2.imprint","INTERSECT",VERTEX,{"derivedFrom":[subQ0,sQuery(id+"F2.wireOp",EDGE,"E13.5.2")]}),-1.0]])],"derivedFrom":subQ0})])],"isStart":true});}
            var Q66;
            Q66=makeQuery(id+"F3.opExtrude","CAP_EDGE",EDGE,{"disambiguationData":[OSD([sQuery(id+"F2.wireOp",EDGE,"E13.5.2")])],"isStart":true});
            var Q67;
            {var subQ0=sQuery(id+"F2.wireOp",EDGE,"E0");Q67=makeQuery(id+"F3.opExtrude","CAP_EDGE",EDGE,{"disambiguationData":[OSD([subQ0]),TDD([makeQuery(id+"F2.imprint","IMPRINT",EDGE,{"disambiguationData":[TD([[makeQuery(id+"F2.imprint","INTERSECT",VERTEX,{"derivedFrom":[subQ0,sQuery(id+"F2.wireOp",EDGE,"E13.4.2")]}),-1.0]])],"derivedFrom":subQ0})])],"isStart":true});}
            var Q68;
            Q68=makeQuery(id+"F3.opExtrude","CAP_EDGE",EDGE,{"disambiguationData":[OSD([sQuery(id+"F2.wireOp",EDGE,"E13.4.2")])],"isStart":true});
            var Q69;
            Q69=makeQuery(id+"F3.opExtrude","CAP_EDGE",EDGE,{"disambiguationData":[OSD([sQuery(id+"F2.wireOp",EDGE,"E13.4.0")])],"isStart":true});
            var Q70;
            {var subQ0=sQuery(id+"F2.wireOp",EDGE,"E0");Q70=makeQuery(id+"F3.opExtrude","CAP_EDGE",EDGE,{"disambiguationData":[OSD([subQ0]),TDD([makeQuery(id+"F2.imprint","IMPRINT",EDGE,{"disambiguationData":[TD([[makeQuery(id+"F2.imprint","INTERSECT",VERTEX,{"derivedFrom":[subQ0,sQuery(id+"F2.wireOp",EDGE,"E13.3.2")]}),-1.0]])],"derivedFrom":subQ0})])],"isStart":true});}
            var Q71;
            Q71=makeQuery(id+"F3.opExtrude","CAP_EDGE",EDGE,{"disambiguationData":[OSD([sQuery(id+"F2.wireOp",EDGE,"E13.3.2")])],"isStart":true});
            var Q72;
            Q72=makeQuery(id+"F3.opExtrude","CAP_EDGE",EDGE,{"disambiguationData":[OSD([sQuery(id+"F2.wireOp",EDGE,"E13.3.0")])],"isStart":true});
            var Q73;
            {var subQ0=sQuery(id+"F2.wireOp",EDGE,"E0");Q73=makeQuery(id+"F3.opExtrude","CAP_EDGE",EDGE,{"disambiguationData":[OSD([subQ0]),TDD([makeQuery(id+"F2.imprint","IMPRINT",EDGE,{"disambiguationData":[TD([[makeQuery(id+"F2.imprint","INTERSECT",VERTEX,{"derivedFrom":[subQ0,sQuery(id+"F2.wireOp",EDGE,"E13.2.2")]}),-1.0]])],"derivedFrom":subQ0})])],"isStart":true});}
            var Q74;
            Q74=makeQuery(id+"F3.opExtrude","CAP_EDGE",EDGE,{"disambiguationData":[OSD([sQuery(id+"F2.wireOp",EDGE,"E13.2.2")])],"isStart":true});
            var Q75;
            Q75=makeQuery(id+"F3.opExtrude","CAP_EDGE",EDGE,{"disambiguationData":[OSD([sQuery(id+"F2.wireOp",EDGE,"E13.2.0")])],"isStart":true});
            var Q76;
            Q76=makeQuery(id+"F3.opExtrude","CAP_EDGE",EDGE,{"disambiguationData":[OSD([sQuery(id+"F2.wireOp",EDGE,"E13.1.2")])],"isStart":true});
            var Q77;
            {var subQ0=sQuery(id+"F2.wireOp",EDGE,"E0");Q77=makeQuery(id+"F3.opExtrude","CAP_EDGE",EDGE,{"disambiguationData":[OSD([subQ0]),TDD([makeQuery(id+"F2.imprint","IMPRINT",EDGE,{"disambiguationData":[TD([[makeQuery(id+"F2.imprint","INTERSECT",VERTEX,{"derivedFrom":[subQ0,sQuery(id+"F2.wireOp",EDGE,"E13.1.2")]}),-1.0]])],"derivedFrom":subQ0})])],"isStart":true});}
            var Q78;
            Q78=makeQuery(id+"F3.opExtrude","CAP_EDGE",EDGE,{"disambiguationData":[OSD([sQuery(id+"F2.wireOp",EDGE,"E13.1.0")])],"isStart":true});
            var Q79;
            {var subQ0=sQuery(id+"F2.wireOp",EDGE,"E0");Q79=makeQuery(id+"F3.opExtrude","CAP_EDGE",EDGE,{"disambiguationData":[OSD([subQ0]),TDD([makeQuery(id+"F2.imprint","IMPRINT",EDGE,{"disambiguationData":[TD([[makeQuery(id+"F2.imprint","INTERSECT",VERTEX,{"derivedFrom":[subQ0,sQuery(id+"F2.wireOp",EDGE,"E11.MirrorCS")]}),-1.0]])],"derivedFrom":subQ0})])],"isStart":true});}
            var Q80;
            Q80=makeQuery(id+"F3.opExtrude","CAP_EDGE",EDGE,{"disambiguationData":[OSD([sQuery(id+"F2.wireOp",EDGE,"E11.MirrorCS")])],"isStart":true});
            var Q81;
            Q81=makeQuery(id+"F3.opExtrude","CAP_EDGE",EDGE,{"disambiguationData":[OSD([sQuery(id+"F2.wireOp",EDGE,"E10.trimOffspring")])],"isStart":true});
            var Q82;
            {var subQ0=sQuery(id+"F2.wireOp",EDGE,"E0");Q82=makeQuery(id+"F3.opExtrude","CAP_EDGE",EDGE,{"disambiguationData":[OSD([subQ0]),TDD([makeQuery(id+"F2.imprint","IMPRINT",EDGE,{"disambiguationData":[TD([[makeQuery(id+"F2.imprint","INTERSECT",VERTEX,{"derivedFrom":[subQ0,sQuery(id+"F2.wireOp",EDGE,"E10.trimOffspring")]}),1.0]])],"derivedFrom":subQ0})])],"isStart":true});}
            var Q83;
            Q83=makeQuery(id+"F3.opExtrude","CAP_EDGE",EDGE,{"disambiguationData":[OSD([sQuery(id+"F2.wireOp",EDGE,"E13.19.2")])],"isStart":true});
            var Q84;
            Q84=makeQuery(id+"F3.opExtrude","CAP_EDGE",EDGE,{"disambiguationData":[OSD([sQuery(id+"F2.wireOp",EDGE,"E13.19.0")])],"isStart":true});
            var Q85;
            {var subQ0=sQuery(id+"F2.wireOp",EDGE,"E0");Q85=makeQuery(id+"F3.opExtrude","CAP_EDGE",EDGE,{"disambiguationData":[OSD([subQ0]),TDD([makeQuery(id+"F2.imprint","IMPRINT",EDGE,{"disambiguationData":[TD([[makeQuery(id+"F2.imprint","INTERSECT",VERTEX,{"derivedFrom":[subQ0,sQuery(id+"F2.wireOp",EDGE,"E13.18.2")]}),-1.0]])],"derivedFrom":subQ0})])],"isStart":true});}
            var Q86;
            Q86=makeQuery(id+"F3.opExtrude","CAP_EDGE",EDGE,{"disambiguationData":[OSD([sQuery(id+"F2.wireOp",EDGE,"E13.18.2")])],"isStart":true});
            var Q87;
            Q87=makeQuery(id+"F3.opExtrude","CAP_EDGE",EDGE,{"disambiguationData":[OSD([sQuery(id+"F2.wireOp",EDGE,"E13.18.0")])],"isStart":true});
            var Q88;
            {var subQ0=sQuery(id+"F2.wireOp",EDGE,"E0");Q88=makeQuery(id+"F3.opExtrude","CAP_EDGE",EDGE,{"disambiguationData":[OSD([subQ0]),TDD([makeQuery(id+"F2.imprint","IMPRINT",EDGE,{"disambiguationData":[TD([[makeQuery(id+"F2.imprint","INTERSECT",VERTEX,{"derivedFrom":[subQ0,sQuery(id+"F2.wireOp",EDGE,"E13.17.2")]}),-1.0]])],"derivedFrom":subQ0})])],"isStart":true});}
            var Q89;
            Q89=makeQuery(id+"F3.opExtrude","CAP_EDGE",EDGE,{"disambiguationData":[OSD([sQuery(id+"F2.wireOp",EDGE,"E13.17.2")])],"isStart":true});
            var Q90;
            Q90=makeQuery(id+"F3.opExtrude","CAP_EDGE",EDGE,{"disambiguationData":[OSD([sQuery(id+"F2.wireOp",EDGE,"E13.17.0")])],"isStart":true});
            var Q91;
            {var subQ0=sQuery(id+"F2.wireOp",EDGE,"E0");Q91=makeQuery(id+"F3.opExtrude","CAP_EDGE",EDGE,{"disambiguationData":[OSD([subQ0]),TDD([makeQuery(id+"F2.imprint","IMPRINT",EDGE,{"disambiguationData":[TD([[makeQuery(id+"F2.imprint","INTERSECT",VERTEX,{"derivedFrom":[subQ0,sQuery(id+"F2.wireOp",EDGE,"E13.16.2")]}),-1.0]])],"derivedFrom":subQ0})])],"isStart":true});}
            var Q92;
            Q92=makeQuery(id+"F3.opExtrude","CAP_EDGE",EDGE,{"disambiguationData":[OSD([sQuery(id+"F2.wireOp",EDGE,"E13.16.2")])],"isStart":true});
            var Q93;
            Q93=makeQuery(id+"F3.opExtrude","CAP_EDGE",EDGE,{"disambiguationData":[OSD([sQuery(id+"F2.wireOp",EDGE,"E13.16.0")])],"isStart":true});
            var Q94;
            {var subQ0=sQuery(id+"F2.wireOp",EDGE,"E0");Q94=makeQuery(id+"F3.opExtrude","CAP_EDGE",EDGE,{"disambiguationData":[OSD([subQ0]),TDD([makeQuery(id+"F2.imprint","IMPRINT",EDGE,{"disambiguationData":[TD([[makeQuery(id+"F2.imprint","INTERSECT",VERTEX,{"derivedFrom":[subQ0,sQuery(id+"F2.wireOp",EDGE,"E13.15.2")]}),-1.0]])],"derivedFrom":subQ0})])],"isStart":true});}
            var Q95;
            Q95=makeQuery(id+"F3.opExtrude","CAP_EDGE",EDGE,{"disambiguationData":[OSD([sQuery(id+"F2.wireOp",EDGE,"E13.15.2")])],"isStart":true});
            var Q96;
            Q96=makeQuery(id+"F3.opExtrude","CAP_EDGE",EDGE,{"disambiguationData":[OSD([sQuery(id+"F2.wireOp",EDGE,"E13.15.0")])],"isStart":true});
            var Q97;
            {var subQ0=sQuery(id+"F2.wireOp",EDGE,"E0");Q97=makeQuery(id+"F3.opExtrude","CAP_EDGE",EDGE,{"disambiguationData":[OSD([subQ0]),TDD([makeQuery(id+"F2.imprint","IMPRINT",EDGE,{"disambiguationData":[TD([[makeQuery(id+"F2.imprint","INTERSECT",VERTEX,{"derivedFrom":[subQ0,sQuery(id+"F2.wireOp",EDGE,"E13.14.2")]}),-1.0]])],"derivedFrom":subQ0})])],"isStart":true});}
            var Q98;
            Q98=makeQuery(id+"F3.opExtrude","CAP_EDGE",EDGE,{"disambiguationData":[OSD([sQuery(id+"F2.wireOp",EDGE,"E13.14.2")])],"isStart":true});
            var Q99;
            Q99=makeQuery(id+"F3.opExtrude","CAP_EDGE",EDGE,{"disambiguationData":[OSD([sQuery(id+"F2.wireOp",EDGE,"E13.14.0")])],"isStart":true});
            var Q100;
            {var subQ0=sQuery(id+"F2.wireOp",EDGE,"E0");Q100=makeQuery(id+"F3.opExtrude","CAP_EDGE",EDGE,{"disambiguationData":[OSD([subQ0]),TDD([makeQuery(id+"F2.imprint","IMPRINT",EDGE,{"disambiguationData":[TD([[makeQuery(id+"F2.imprint","INTERSECT",VERTEX,{"derivedFrom":[subQ0,sQuery(id+"F2.wireOp",EDGE,"E13.13.2")]}),-1.0]])],"derivedFrom":subQ0})])],"isStart":true});}
            var Q101;
            Q101=makeQuery(id+"F3.opExtrude","CAP_EDGE",EDGE,{"disambiguationData":[OSD([sQuery(id+"F2.wireOp",EDGE,"E13.13.2")])],"isStart":true});
            var Q102;
            Q102=makeQuery(id+"F3.opExtrude","CAP_EDGE",EDGE,{"disambiguationData":[OSD([sQuery(id+"F2.wireOp",EDGE,"E13.13.0")])],"isStart":true});
            var Q103;
            {var subQ0=sQuery(id+"F2.wireOp",EDGE,"E0");Q103=makeQuery(id+"F3.opExtrude","CAP_EDGE",EDGE,{"disambiguationData":[OSD([subQ0]),TDD([makeQuery(id+"F2.imprint","IMPRINT",EDGE,{"disambiguationData":[TD([[makeQuery(id+"F2.imprint","INTERSECT",VERTEX,{"derivedFrom":[subQ0,sQuery(id+"F2.wireOp",EDGE,"E13.12.2")]}),-1.0]])],"derivedFrom":subQ0})])],"isStart":true});}
            var Q104;
            Q104=makeQuery(id+"F3.opExtrude","CAP_EDGE",EDGE,{"disambiguationData":[OSD([sQuery(id+"F2.wireOp",EDGE,"E13.12.2")])],"isStart":true});
            var Q105;
            Q105=makeQuery(id+"F3.opExtrude","CAP_EDGE",EDGE,{"disambiguationData":[OSD([sQuery(id+"F2.wireOp",EDGE,"E13.12.0")])],"isStart":true});
            var Q106;
            {var subQ0=sQuery(id+"F2.wireOp",EDGE,"E0");Q106=makeQuery(id+"F3.opExtrude","CAP_EDGE",EDGE,{"disambiguationData":[OSD([subQ0]),TDD([makeQuery(id+"F2.imprint","IMPRINT",EDGE,{"disambiguationData":[TD([[makeQuery(id+"F2.imprint","INTERSECT",VERTEX,{"derivedFrom":[subQ0,sQuery(id+"F2.wireOp",EDGE,"E13.11.2")]}),-1.0]])],"derivedFrom":subQ0})])],"isStart":true});}
            var Q107;
            Q107=makeQuery(id+"F3.opExtrude","CAP_EDGE",EDGE,{"disambiguationData":[OSD([sQuery(id+"F2.wireOp",EDGE,"E13.11.2")])],"isStart":true});
            var Q108;
            Q108=makeQuery(id+"F3.opExtrude","CAP_EDGE",EDGE,{"disambiguationData":[OSD([sQuery(id+"F2.wireOp",EDGE,"E13.11.0")])],"isStart":true});
            var Q109;
            {var subQ0=sQuery(id+"F2.wireOp",EDGE,"E0");Q109=makeQuery(id+"F3.opExtrude","CAP_EDGE",EDGE,{"disambiguationData":[OSD([subQ0]),TDD([makeQuery(id+"F2.imprint","IMPRINT",EDGE,{"disambiguationData":[TD([[makeQuery(id+"F2.imprint","INTERSECT",VERTEX,{"derivedFrom":[subQ0,sQuery(id+"F2.wireOp",EDGE,"E13.10.2")]}),-1.0]])],"derivedFrom":subQ0})])],"isStart":true});}
            var Q110;
            Q110=makeQuery(id+"F3.opExtrude","CAP_EDGE",EDGE,{"disambiguationData":[OSD([sQuery(id+"F2.wireOp",EDGE,"E13.10.2")])],"isStart":true});
            var Q111;
            Q111=makeQuery(id+"F3.opExtrude","CAP_EDGE",EDGE,{"disambiguationData":[OSD([sQuery(id+"F2.wireOp",EDGE,"E13.10.0")])],"isStart":true});
            var Q112;
            {var subQ0=sQuery(id+"F2.wireOp",EDGE,"E0");Q112=makeQuery(id+"F3.opExtrude","CAP_EDGE",EDGE,{"disambiguationData":[OSD([subQ0]),TDD([makeQuery(id+"F2.imprint","IMPRINT",EDGE,{"disambiguationData":[TD([[makeQuery(id+"F2.imprint","INTERSECT",VERTEX,{"derivedFrom":[subQ0,sQuery(id+"F2.wireOp",EDGE,"E13.9.2")]}),-1.0]])],"derivedFrom":subQ0})])],"isStart":true});}
            var Q113;
            Q113=makeQuery(id+"F3.opExtrude","CAP_EDGE",EDGE,{"disambiguationData":[OSD([sQuery(id+"F2.wireOp",EDGE,"E13.9.2")])],"isStart":true});
            var Q114;
            Q114=makeQuery(id+"F3.opExtrude","CAP_EDGE",EDGE,{"disambiguationData":[OSD([sQuery(id+"F2.wireOp",EDGE,"E13.9.0")])],"isStart":true});
            var Q115;
            {var subQ0=sQuery(id+"F2.wireOp",EDGE,"E0");Q115=makeQuery(id+"F3.opExtrude","CAP_EDGE",EDGE,{"disambiguationData":[OSD([subQ0]),TDD([makeQuery(id+"F2.imprint","IMPRINT",EDGE,{"disambiguationData":[TD([[makeQuery(id+"F2.imprint","INTERSECT",VERTEX,{"derivedFrom":[subQ0,sQuery(id+"F2.wireOp",EDGE,"E13.8.2")]}),-1.0]])],"derivedFrom":subQ0})])],"isStart":true});}
            var Q116;
            Q116=makeQuery(id+"F3.opExtrude","CAP_EDGE",EDGE,{"disambiguationData":[OSD([sQuery(id+"F2.wireOp",EDGE,"E13.8.2")])],"isStart":true});
            fillet(context, id + "F4", {"entities" : qUnion([Q0, Q1, Q2, Q3, Q4, Q5, Q6, Q7, Q8, Q9, Q10, Q11, Q12, Q13, Q14, Q15, Q16, Q17, Q18, Q19, Q20, Q21, Q22, Q23, Q24, Q25, Q26, Q27, Q28, Q29, Q30, Q31, Q32, Q33, Q34, Q35, Q36, Q37, Q38, Q39, Q40, Q41, Q42, Q43, Q44, Q45, Q46, Q47, Q48, Q49, Q50, Q51, Q52, Q53, Q54, Q55, Q56, Q57, Q58, Q59, Q60, Q61, Q62, Q63, Q64, Q65, Q66, Q67, Q68, Q69, Q70, Q71, Q72, Q73, Q74, Q75, Q76, Q77, Q78, Q79, Q80, Q81, Q82, Q83, Q84, Q85, Q86, Q87, Q88, Q89, Q90, Q91, Q92, Q93, Q94, Q95, Q96, Q97, Q98, Q99, Q100, Q101, Q102, Q103, Q104, Q105, Q106, Q107, Q108, Q109, Q110, Q111, Q112, Q113, Q114, Q115, Q116]), "radius" : (getVariable(context, 'TeethFillet')) * mm, "tangentPropagation" : true, "allowEdgeOverflow" : false});
        }
    });
